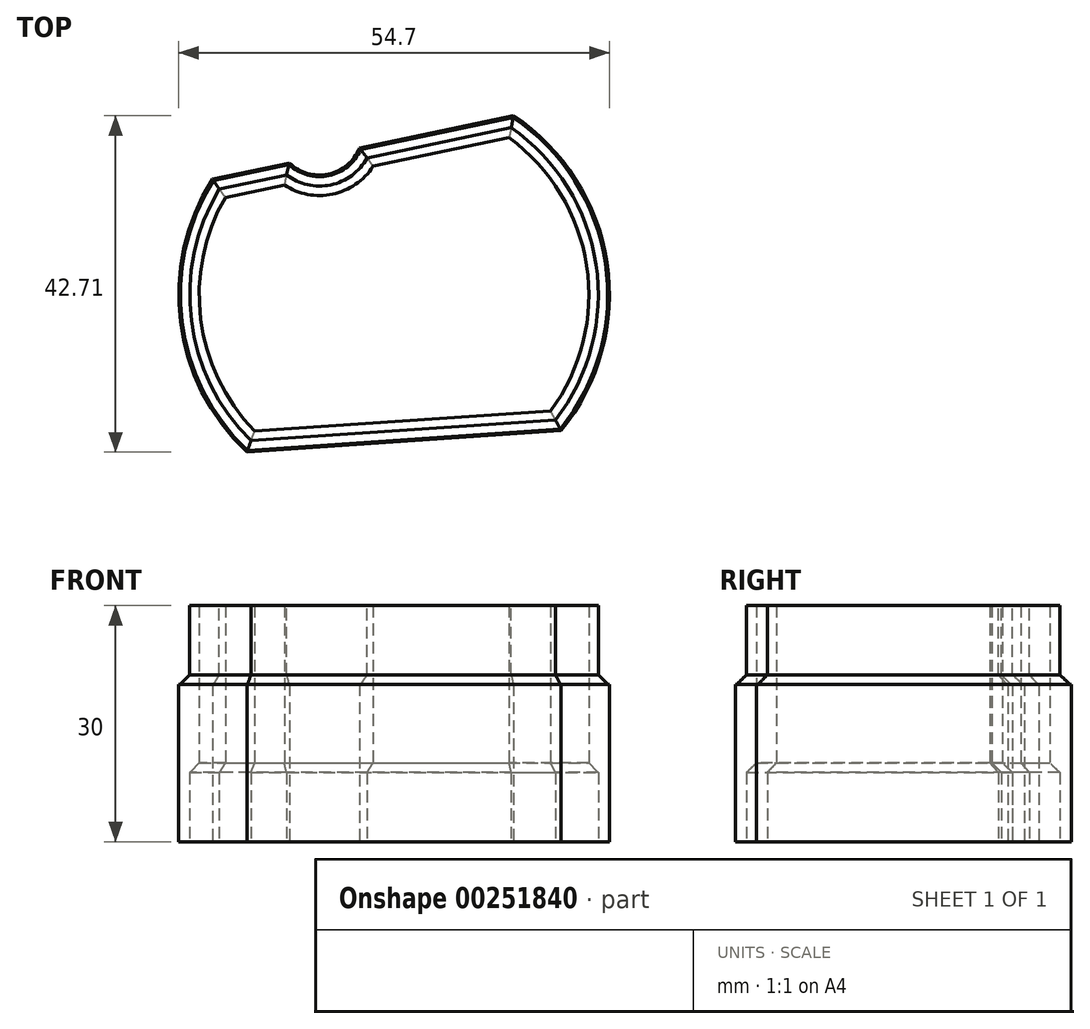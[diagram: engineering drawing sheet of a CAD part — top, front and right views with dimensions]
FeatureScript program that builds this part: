
annotation { "Feature Type Name" : "Feature", "Feature Type Description" : "" }
export const myFeature = defineFeature(function(context is Context, id is Id, definition is map)
    precondition{}
    {
        {
            var Q0;
            Q0=qCreatedBy(makeId("Top.planeOp"),FACE);
            var sketch = newSketch(context, id + "F0", { "sketchPlane" : qUnion([Q0])});
            skArc(sketch, "E0", {"start": v(30.7, -14.7) * mm, "mid": v(36.51, 6.64) * mm, "end": v(24.66, 25.3) * mm});
            skArc(sketch, "E1.trimOffspring", {"start": v(-13.6, 17.25) * mm, "mid": v(-17.66, -0.87) * mm, "end": v(-9.22, -17.41) * mm});
            skLineSegment(sketch, "E2", {"start": v(-13.6, 17.25) * mm, "end": v(-3.8, 19.3) * mm});
            skLineSegment(sketch, "E3.trimOffspring", {"start": v(30.7, -14.7) * mm, "end": v(30.7, -14.7) * mm});
            skLineSegment(sketch, "E4", {"start": v(-9.22, -17.41) * mm, "end": v(30.7, -14.7) * mm});
            skArc(sketch, "E5", {"start": v(-3.8, 19.3) * mm, "mid": v(1.13, 17.9) * mm, "end": v(5.08, 21.18) * mm});
            skLineSegment(sketch, "E6.trimOffspring", {"start": v(5.08, 21.18) * mm, "end": v(24.66, 25.3) * mm});
            skLineSegment(sketch, "E7.0", {"start": v(-11.96, 14.94) * mm, "end": v(-4.46, 16.52) * mm});
            skLineSegment(sketch, "E7.1", {"start": v(-8.23, -14.74) * mm, "end": v(29.35, -12.18) * mm});
            skArc(sketch, "E7.2", {"start": v(29.35, -12.18) * mm, "mid": v(33.94, 6.27) * mm, "end": v(24.09, 22.53) * mm});
            skArc(sketch, "E7.3", {"start": v(-11.96, 14.94) * mm, "mid": v(-15.08, -0.53) * mm, "end": v(-8.23, -14.74) * mm});
            skLineSegment(sketch, "E7.4", {"start": v(6.8, 18.89) * mm, "end": v(24.09, 22.53) * mm});
            skArc(sketch, "E7.5", {"start": v(-4.46, 16.52) * mm, "mid": v(1.67, 15.35) * mm, "end": v(6.8, 18.89) * mm});
            skSolve(sketch);
        }
        {
            var Q0;
            Q0=makeQuery(id+"F0.imprint","IMPRINT",FACE,{"disambiguationData":[TD([[makeQuery(id+"F0.imprint","IMPRINT",EDGE,{"derivedFrom":sQuery(id+"F0.wireOp",EDGE,"E0")}),1.0]])]});
            extrude(context, id + "F1", {"entities" : qUnion([Q0]), "depth" : 30 * mm});
        }
        {
            var Q0;
            Q0=makeQuery(id+"F1.opExtrude","CAP_FACE",FACE,{"disambiguationData":[OSD([sQuery(id+"F0.wireOp",EDGE,"E0"),sQuery(id+"F0.wireOp",EDGE,"E1.trimOffspring"),sQuery(id+"F0.wireOp",EDGE,"E2"),sQuery(id+"F0.wireOp",EDGE,"E4"),sQuery(id+"F0.wireOp",EDGE,"E5"),sQuery(id+"F0.wireOp",EDGE,"E6.trimOffspring"),sQuery(id+"F0.wireOp",EDGE,"E7.0"),sQuery(id+"F0.wireOp",EDGE,"E7.1"),sQuery(id+"F0.wireOp",EDGE,"E7.2"),sQuery(id+"F0.wireOp",EDGE,"E7.3"),sQuery(id+"F0.wireOp",EDGE,"E7.4"),sQuery(id+"F0.wireOp",EDGE,"E7.5")])],"isStart":true});
            var sketch = newSketch(context, id + "F2", { "sketchPlane" : qUnion([Q0])});
            skArc(sketch, "E8.0", {"start": v(-4.2, -17.8) * mm, "mid": v(1.42, -16.53) * mm, "end": v(6.05, -19.95) * mm});
            skArc(sketch, "E8.1", {"start": v(29.98, 13.34) * mm, "mid": v(35.13, -6.44) * mm, "end": v(24.36, -23.8) * mm});
            skLineSegment(sketch, "E8.2", {"start": v(-8.7, 15.97) * mm, "end": v(29.98, 13.34) * mm});
            skLineSegment(sketch, "E8.3", {"start": v(6.05, -19.95) * mm, "end": v(24.36, -23.8) * mm});
            skArc(sketch, "E8.4", {"start": v(-12.72, -16) * mm, "mid": v(-16.27, 0.69) * mm, "end": v(-8.7, 15.97) * mm});
            skLineSegment(sketch, "E8.5", {"start": v(-12.72, -16) * mm, "end": v(-4.2, -17.8) * mm});
            skSolve(sketch);
        }
        {
            var Q0;
            Q0=makeQuery(id+"F2.imprint","IMPRINT",FACE,{"disambiguationData":[TD([[makeQuery(id+"F2.imprint","IMPRINT",EDGE,{"derivedFrom":sQuery(id+"F2.wireOp",EDGE,"E8.0")}),-1.0]])]});
            extrude(context, id + "F3", {"entities" : qUnion([Q0]), "operationType" : NewBodyOperationType.REMOVE, "oppositeDirection" : true, "depth" : 10 * mm});
        }
        {
            var Q0;
            Q0=makeQuery(id+"F1.opExtrude","CAP_FACE",FACE,{"disambiguationData":[OSD([sQuery(id+"F0.wireOp",EDGE,"E0"),sQuery(id+"F0.wireOp",EDGE,"E1.trimOffspring"),sQuery(id+"F0.wireOp",EDGE,"E2"),sQuery(id+"F0.wireOp",EDGE,"E4"),sQuery(id+"F0.wireOp",EDGE,"E5"),sQuery(id+"F0.wireOp",EDGE,"E6.trimOffspring"),sQuery(id+"F0.wireOp",EDGE,"E7.0"),sQuery(id+"F0.wireOp",EDGE,"E7.1"),sQuery(id+"F0.wireOp",EDGE,"E7.2"),sQuery(id+"F0.wireOp",EDGE,"E7.3"),sQuery(id+"F0.wireOp",EDGE,"E7.4"),sQuery(id+"F0.wireOp",EDGE,"E7.5")])],"isStart":false});
            var sketch = newSketch(context, id + "F4", { "sketchPlane" : qUnion([Q0])});
            skArc(sketch, "E9.0", {"start": v(-12.72, 16) * mm, "mid": v(-16.27, -0.69) * mm, "end": v(-8.7, -15.97) * mm});
            skArc(sketch, "E9.1", {"start": v(-4.2, 17.8) * mm, "mid": v(1.42, 16.53) * mm, "end": v(6.05, 19.95) * mm});
            skLineSegment(sketch, "E9.2", {"start": v(6.05, 19.95) * mm, "end": v(24.36, 23.8) * mm});
            skLineSegment(sketch, "E9.3", {"start": v(-12.72, 16) * mm, "end": v(-4.2, 17.8) * mm});
            skArc(sketch, "E9.4", {"start": v(29.98, -13.34) * mm, "mid": v(35.13, 6.44) * mm, "end": v(24.36, 23.8) * mm});
            skLineSegment(sketch, "E9.5", {"start": v(-8.7, -15.97) * mm, "end": v(29.98, -13.34) * mm});
            skSolve(sketch);
        }
        {
            var Q0;
            Q0=makeQuery(id+"F4.imprint","IMPRINT",FACE,{"disambiguationData":[TD([[makeQuery(id+"F4.imprint","IMPRINT",EDGE,{"derivedFrom":sQuery(id+"F4.wireOp",EDGE,"E9.0")}),-1.0]])]});
            extrude(context, id + "F5", {"entities" : qUnion([Q0]), "operationType" : NewBodyOperationType.REMOVE, "oppositeDirection" : true, "depth" : 10 * mm});
        }
        {
            var Q0;
            Q0=makeQuery(id+"F5.boolean.opBoolean","COPY",EDGE,{"derivedFrom":makeQuery(id+"F5.opExtrude","CAP_EDGE",EDGE,{"disambiguationData":[OSD([sQuery(id+"F4.wireOp",EDGE,"E9.0")])],"isStart":false})});
            var Q1;
            Q1=makeQuery(id+"F5.boolean.opBoolean","COPY",EDGE,{"derivedFrom":makeQuery(id+"F5.opExtrude","CAP_EDGE",EDGE,{"disambiguationData":[OSD([sQuery(id+"F4.wireOp",EDGE,"E9.3")])],"isStart":false})});
            var Q2;
            Q2=makeQuery(id+"F5.boolean.opBoolean","COPY",EDGE,{"derivedFrom":makeQuery(id+"F5.opExtrude","CAP_EDGE",EDGE,{"disambiguationData":[OSD([sQuery(id+"F4.wireOp",EDGE,"E9.1")])],"isStart":false})});
            var Q3;
            Q3=makeQuery(id+"F5.boolean.opBoolean","COPY",EDGE,{"derivedFrom":makeQuery(id+"F5.opExtrude","CAP_EDGE",EDGE,{"disambiguationData":[OSD([sQuery(id+"F4.wireOp",EDGE,"E9.2")])],"isStart":false})});
            var Q4;
            Q4=makeQuery(id+"F5.boolean.opBoolean","COPY",EDGE,{"derivedFrom":makeQuery(id+"F5.opExtrude","CAP_EDGE",EDGE,{"disambiguationData":[OSD([sQuery(id+"F4.wireOp",EDGE,"E9.4")])],"isStart":false})});
            var Q5;
            Q5=makeQuery(id+"F5.boolean.opBoolean","COPY",EDGE,{"derivedFrom":makeQuery(id+"F5.opExtrude","CAP_EDGE",EDGE,{"disambiguationData":[OSD([sQuery(id+"F4.wireOp",EDGE,"E9.5")])],"isStart":false})});
            var Q6;
            Q6=makeQuery(id+"F3.boolean.opBoolean","COPY",EDGE,{"derivedFrom":makeQuery(id+"F3.opExtrude","CAP_EDGE",EDGE,{"disambiguationData":[OSD([sQuery(id+"F2.wireOp",EDGE,"E8.3")])],"isStart":false})});
            var Q7;
            Q7=makeQuery(id+"F3.boolean.opBoolean","COPY",EDGE,{"derivedFrom":makeQuery(id+"F3.opExtrude","CAP_EDGE",EDGE,{"disambiguationData":[OSD([sQuery(id+"F2.wireOp",EDGE,"E8.1")])],"isStart":false})});
            var Q8;
            Q8=makeQuery(id+"F3.boolean.opBoolean","COPY",EDGE,{"derivedFrom":makeQuery(id+"F3.opExtrude","CAP_EDGE",EDGE,{"disambiguationData":[OSD([sQuery(id+"F2.wireOp",EDGE,"E8.0")])],"isStart":false})});
            var Q9;
            Q9=makeQuery(id+"F3.boolean.opBoolean","COPY",EDGE,{"derivedFrom":makeQuery(id+"F3.opExtrude","CAP_EDGE",EDGE,{"disambiguationData":[OSD([sQuery(id+"F2.wireOp",EDGE,"E8.5")])],"isStart":false})});
            var Q10;
            Q10=makeQuery(id+"F3.boolean.opBoolean","COPY",EDGE,{"derivedFrom":makeQuery(id+"F3.opExtrude","CAP_EDGE",EDGE,{"disambiguationData":[OSD([sQuery(id+"F2.wireOp",EDGE,"E8.4")])],"isStart":false})});
            var Q11;
            Q11=makeQuery(id+"F3.boolean.opBoolean","COPY",EDGE,{"derivedFrom":makeQuery(id+"F3.opExtrude","CAP_EDGE",EDGE,{"disambiguationData":[OSD([sQuery(id+"F2.wireOp",EDGE,"E8.2")])],"isStart":false})});
            chamfer(context, id + "F6", {"entities" : qUnion([Q0, Q1, Q2, Q3, Q4, Q5, Q6, Q7, Q8, Q9, Q10, Q11]), "width" : 1.2 * mm, "tangentPropagation" : true});
        }
    });
